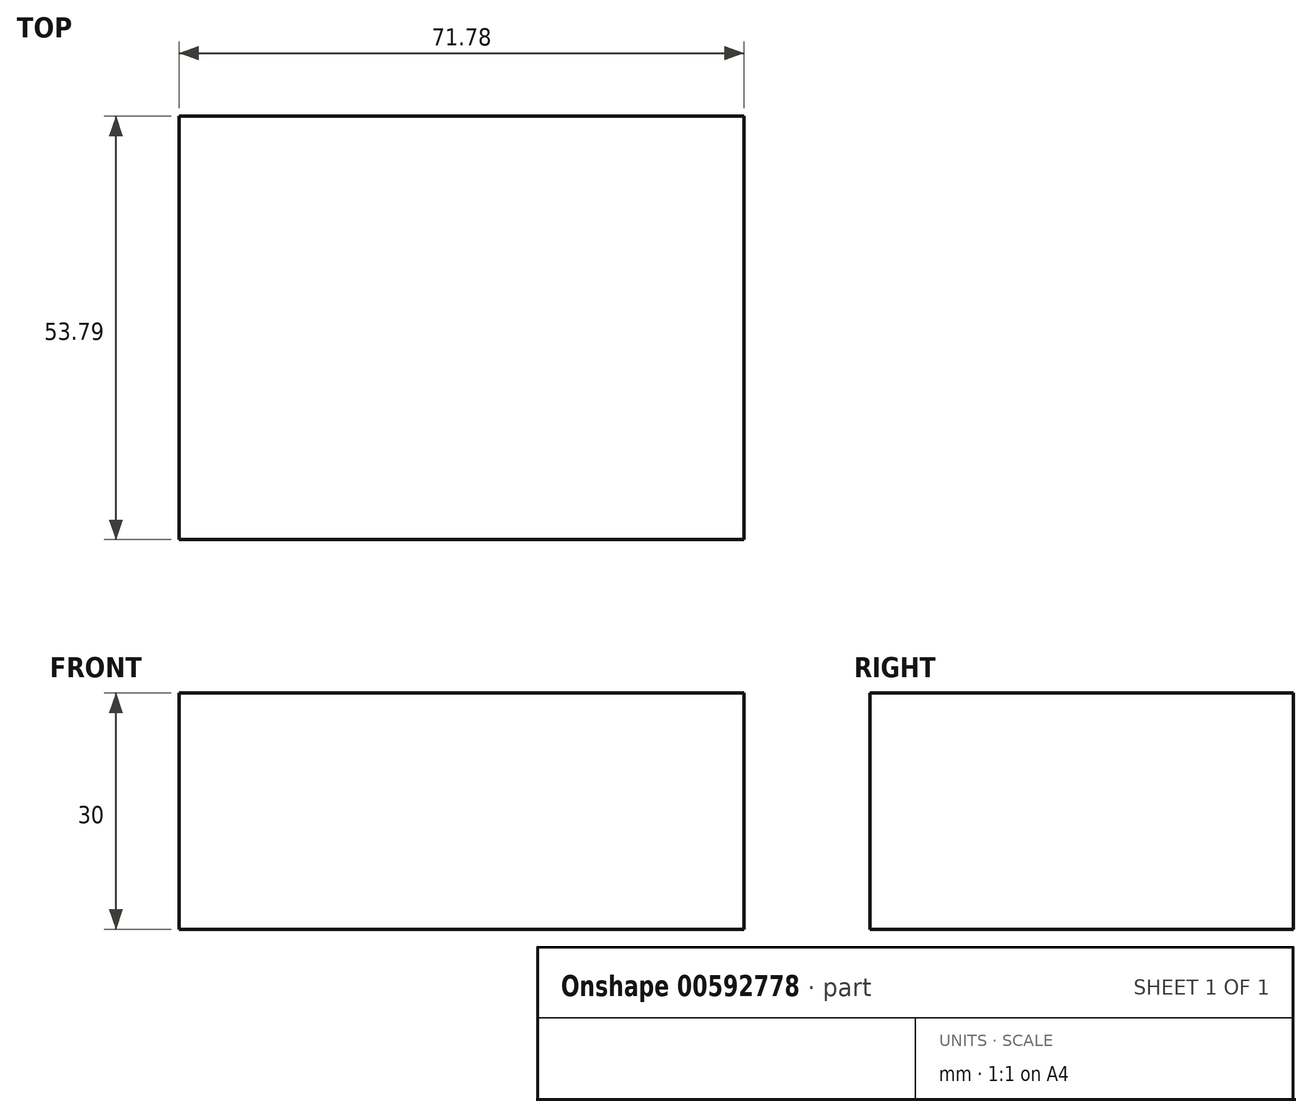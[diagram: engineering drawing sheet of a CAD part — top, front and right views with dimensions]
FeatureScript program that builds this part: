
annotation { "Feature Type Name" : "Feature", "Feature Type Description" : "" }
export const myFeature = defineFeature(function(context is Context, id is Id, definition is map)
    precondition{}
    {
        {
            var Q0;
            Q0=qCreatedBy(makeId("Top.planeOp"),FACE);
            var sketch = newSketch(context, id + "F0", { "sketchPlane" : qUnion([Q0])});
            skLineSegment(sketch, "E0.bottom", {"start": v(-31.45, -20.48) * mm, "end": v(40.33, -20.48) * mm});
            skLineSegment(sketch, "E0.top", {"start": v(-31.45, 33.31) * mm, "end": v(40.33, 33.31) * mm});
            skLineSegment(sketch, "E0.left", {"start": v(-31.45, -20.48) * mm, "end": v(-31.45, 33.31) * mm});
            skLineSegment(sketch, "E0.right", {"start": v(40.33, -20.48) * mm, "end": v(40.33, 33.31) * mm});
            skSolve(sketch);
        }
        {
            var Q0;
            Q0=makeQuery(id+"F0.imprint","IMPRINT",FACE,{"disambiguationData":[TD([[makeQuery(id+"F0.imprint","IMPRINT",EDGE,{"derivedFrom":sQuery(id+"F0.wireOp",EDGE,"E0.bottom")}),1.0]])]});
            extrude(context, id + "F1", {"entities" : qUnion([Q0]), "oppositeDirection" : true, "depth" : 30 * mm, "offsetDistance" : 25.4 * mm});
        }
    });
